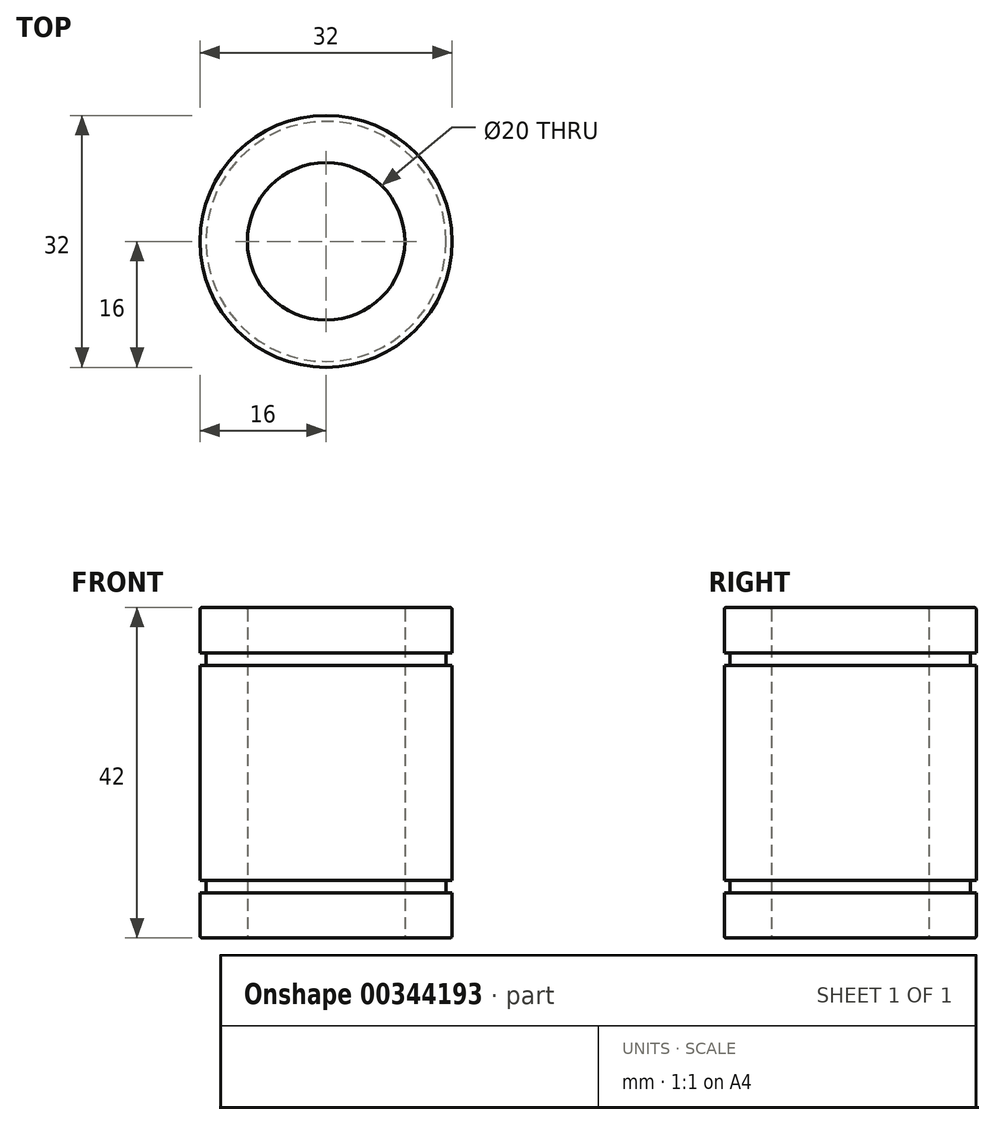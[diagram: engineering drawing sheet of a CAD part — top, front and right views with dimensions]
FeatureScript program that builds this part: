
annotation { "Feature Type Name" : "Feature", "Feature Type Description" : "" }
export const myFeature = defineFeature(function(context is Context, id is Id, definition is map)
    precondition{}
    {
        {
            var Q0;
            Q0=qCreatedBy(makeId("Top.planeOp"),FACE);
            var sketch = newSketch(context, id + "F0", { "sketchPlane" : qUnion([Q0])});
            skCircle(sketch, "E0", {"center": v(0, 0) * mm, "radius": 10 * mm});
            skCircle(sketch, "E1", {"center": v(0, 0) * mm, "radius": 16 * mm});
            skSolve(sketch);
        }
        {
            var Q0;
            Q0=qSketchRegion(id+"F0",true);
            extrude(context, id + "F1", {"entities" : qUnion([Q0]), "depth" : 42 * mm});
        }
        {
            var Q0;
            Q0=makeQuery(id+"F1.opExtrude","CAP_FACE",FACE,{"disambiguationData":[OSD([sQuery(id+"F0.wireOp",EDGE,"E0"),sQuery(id+"F0.wireOp",EDGE,"E1")])],"isStart":false});
            var Q1;
            Q1=makeQuery(id+"F1.opExtrude","CAP_FACE",FACE,{"disambiguationData":[OSD([sQuery(id+"F0.wireOp",EDGE,"E0"),sQuery(id+"F0.wireOp",EDGE,"E1")])],"isStart":true});
            fillet(context, id + "F2", {"entities" : qUnion([Q0, Q1]), "radius" : .25 * mm, "tangentPropagation" : true, "allowEdgeOverflow" : false});
        }
        {
            var Q0;
            Q0=makeQuery(id+"F1.opExtrude","CAP_FACE",FACE,{"disambiguationData":[OSD([sQuery(id+"F0.wireOp",EDGE,"E0"),sQuery(id+"F0.wireOp",EDGE,"E1")])],"isStart":false});
            var sketch = newSketch(context, id + "F3", { "sketchPlane" : qUnion([Q0])});
            skCircle(sketch, "E2", {"center": v(0, 0) * mm, "radius": 15.25 * mm});
            skCircle(sketch, "E3", {"center": v(0, 0) * mm, "radius": 16 * mm});
            skSolve(sketch);
        }
        {
            var Q0;
            Q0=qSketchRegion(id+"F3",true);
            extrude(context, id + "F4", {"entities" : qUnion([Q0]), "operationType" : NewBodyOperationType.REMOVE, "oppositeDirection" : true, "depth" : 7.35 * mm, "hasSecondDirection" : true, "secondDirectionOppositeDirection" : true, "secondDirectionDepth" : 5.75 * mm});
        }
        {
            var Q0;
            Q0=qSketchRegion(id+"F3",true);
            extrude(context, id + "F5", {"entities" : qUnion([Q0]), "operationType" : NewBodyOperationType.REMOVE, "oppositeDirection" : true, "depth" : 36.25 * mm, "hasSecondDirection" : true, "secondDirectionOppositeDirection" : true, "secondDirectionDepth" : 34.65 * mm});
        }
    });
